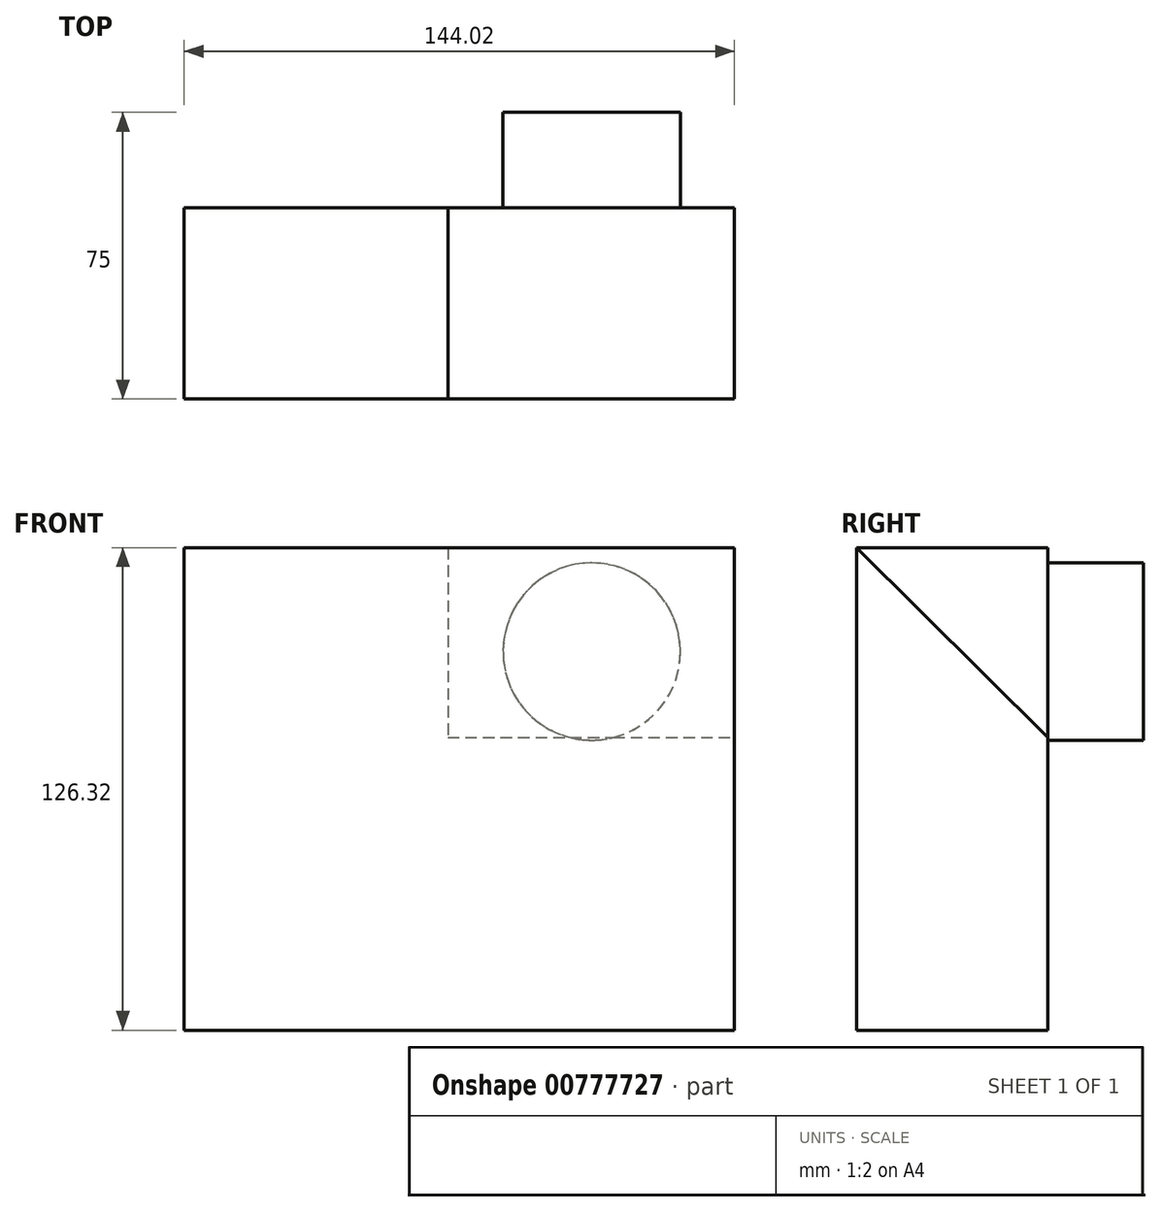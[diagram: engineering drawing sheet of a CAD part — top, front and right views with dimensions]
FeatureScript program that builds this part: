
annotation { "Feature Type Name" : "Feature", "Feature Type Description" : "" }
export const myFeature = defineFeature(function(context is Context, id is Id, definition is map)
    precondition{}
    {
        {
            var Q0;
            Q0=qCreatedBy(makeId("Front.planeOp"),FACE);
            var sketch = newSketch(context, id + "F0", { "sketchPlane" : qUnion([Q0])});
            skLineSegment(sketch, "E0.bottom", {"start": v(-70.56, 53.37) * mm, "end": v(73.46, 53.37) * mm});
            skLineSegment(sketch, "E0.top", {"start": v(-70.56, -72.95) * mm, "end": v(73.46, -72.95) * mm});
            skLineSegment(sketch, "E0.left", {"start": v(-70.56, 53.37) * mm, "end": v(-70.56, -72.95) * mm});
            skLineSegment(sketch, "E0.right", {"start": v(73.46, 53.37) * mm, "end": v(73.46, -72.95) * mm});
            skSolve(sketch);
        }
        {
            var Q0;
            Q0=makeQuery(id+"F0.imprint","IMPRINT",FACE,{"disambiguationData":[TD([[makeQuery(id+"F0.imprint","IMPRINT",EDGE,{"derivedFrom":sQuery(id+"F0.wireOp",EDGE,"E0.bottom")}),-1.0]])]});
            extrude(context, id + "F1", {"entities" : qUnion([Q0]), "depth" : 50 * mm, "offsetDistance" : 25 * mm});
        }
        {
            var Q0;
            Q0=makeQuery(id+"F1.opExtrude","SWEPT_FACE",FACE,{"disambiguationData":[OSD([sQuery(id+"F0.wireOp",EDGE,"E0.right")])]});
            var sketch = newSketch(context, id + "F2", { "sketchPlane" : qUnion([Q0])});
            skLineSegment(sketch, "E1", {"start": v(-50, 53.37) * mm, "end": v(0, 3.68) * mm});
            skSolve(sketch);
        }
        {
            var Q0;
            {var subQ0=sQuery(id+"F2.wireOp",EDGE,"E1");Q0=makeQuery(id+"F2.imprint","IMPRINT",FACE,{"disambiguationData":[TD([[makeQuery(id+"F2.imprint","IMPRINT",EDGE,{"derivedFrom":subQ0}),1.0]])]});}
            extrude(context, id + "F3", {"entities" : qUnion([Q0]), "operationType" : NewBodyOperationType.REMOVE, "oppositeDirection" : true, "depth" : 75 * mm, "offsetDistance" : 25 * mm});
        }
        {
            var Q0;
            Q0=makeQuery(id+"F0.imprint","IMPRINT",FACE,{"disambiguationData":[TD([[makeQuery(id+"F0.imprint","IMPRINT",EDGE,{"derivedFrom":sQuery(id+"F0.wireOp",EDGE,"E0.bottom")}),-1.0]])]});
            var sketch = newSketch(context, id + "F4", { "sketchPlane" : qUnion([Q0])});
            skCircle(sketch, "E2", {"center": v(36.1, 26.19) * mm, "radius": 23.2 * mm});
            skSolve(sketch);
        }
        {
            var Q0;
            Q0 = qSketchRegion(id + "F4", true);
            extrude(context, id + "F5", {"entities" : qUnion([Q0]), "operationType" : NewBodyOperationType.ADD, "oppositeDirection" : true, "depth" : 25 * mm, "offsetDistance" : 25 * mm});
        }
    });
